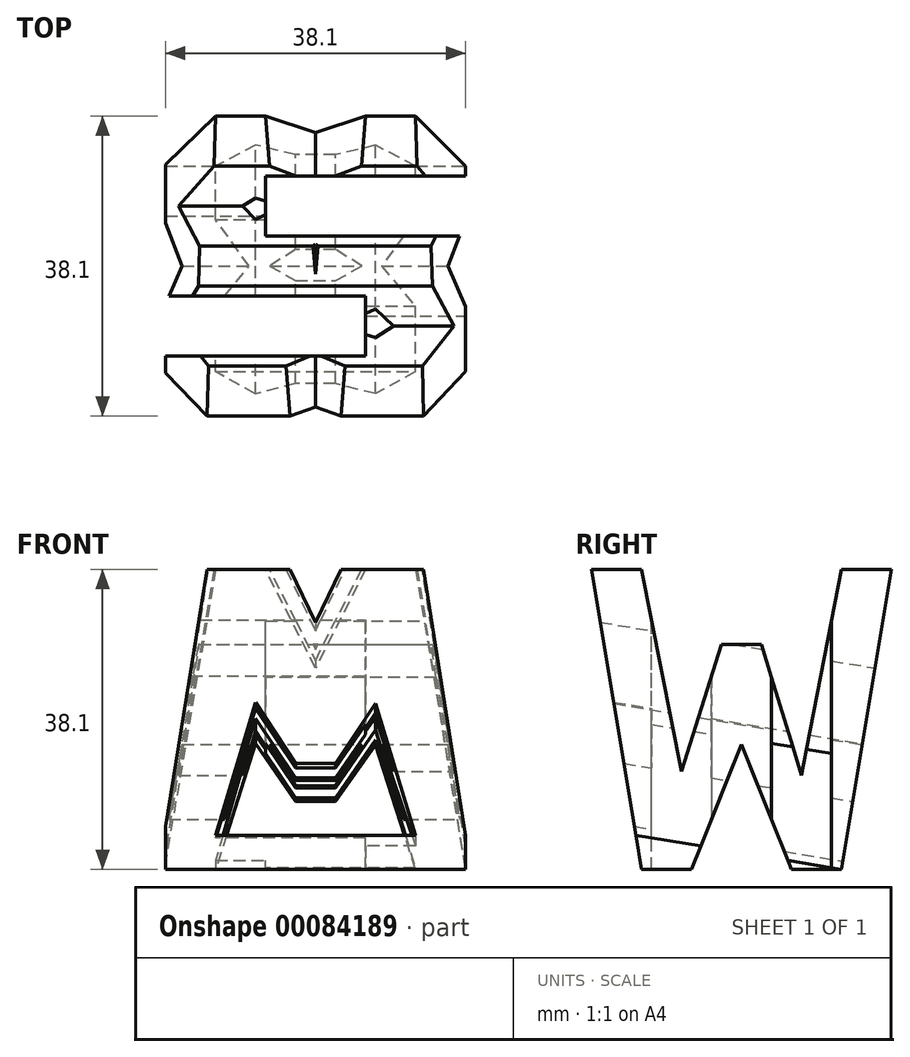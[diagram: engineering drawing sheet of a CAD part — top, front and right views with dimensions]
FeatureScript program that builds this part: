
annotation { "Feature Type Name" : "Feature", "Feature Type Description" : "" }
export const myFeature = defineFeature(function(context is Context, id is Id, definition is map)
    precondition{}
    {
        {
            var Q0;
            Q0=qCreatedBy(makeId("Front.planeOp"),FACE);
            var sketch = newSketch(context, id + "F0", { "sketchPlane" : qUnion([Q0])});
            skLineSegment(sketch, "E0", {"start": v(0, 0) * mm, "end": v(38.1, 0) * mm});
            skLineSegment(sketch, "E1", {"start": v(38.1, 0) * mm, "end": v(38.1, 38.1) * mm});
            skLineSegment(sketch, "E2", {"start": v(38.1, 38.1) * mm, "end": v(0, 38.1) * mm});
            skLineSegment(sketch, "E3", {"start": v(0, 38.1) * mm, "end": v(0, 0) * mm});
            skSolve(sketch);
        }
        {
            var Q0;
            Q0=makeQuery(id+"F0.imprint","IMPRINT",FACE,{"disambiguationData":[TD([[makeQuery(id+"F0.imprint","IMPRINT",EDGE,{"derivedFrom":sQuery(id+"F0.wireOp",EDGE,"E0")}),1.0]])]});
            extrude(context, id + "F1", {"entities" : qUnion([Q0]), "depth" : 38.1 * mm});
        }
        {
            var Q0;
            Q0=qCreatedBy(makeId("Top.planeOp"),FACE);
            cPlane(context, id + "F2", {"entities" : qUnion([Q0]), "cplaneType" : CPlaneType.OFFSET, "offset" : 38.1 * mm, "width" : 152.4 * mm, "height" : 152.4 * mm});
        }
        {
            var Q0;
            Q0=makeQuery(id+"F1.opExtrude","SWEPT_FACE",FACE,{"disambiguationData":[OSD([sQuery(id+"F0.wireOp",EDGE,"E1")])]});
            var sketch = newSketch(context, id + "F3", { "sketchPlane" : qUnion([Q0])});
            skLineSegment(sketch, "E4", {"start": v(-31.75, 38.1) * mm, "end": v(-26.67, 12.44) * mm});
            skLineSegment(sketch, "E5", {"start": v(-26.67, 12.44) * mm, "end": v(-21.6, 28.58) * mm});
            skLineSegment(sketch, "E6", {"start": v(-21.59, 28.58) * mm, "end": v(-16.5, 28.58) * mm});
            skLineSegment(sketch, "E7", {"start": v(-16.5, 28.58) * mm, "end": v(-11.43, 11.92) * mm});
            skLineSegment(sketch, "E8", {"start": v(-11.43, 11.92) * mm, "end": v(-6.35, 38.1) * mm});
            skLineSegment(sketch, "E9", {"start": v(-6.35, 38.1) * mm, "end": v(0, 38.1) * mm});
            skLineSegment(sketch, "E10", {"start": v(0, 38.1) * mm, "end": v(-6.35, 0) * mm});
            skLineSegment(sketch, "E11", {"start": v(-12.7, 0) * mm, "end": v(-19.05, 15.88) * mm});
            skPoint(sketch, "E11.endSnap0", {"position": v(-19.05, 0) * mm});
            skLineSegment(sketch, "E12", {"start": v(-19.05, 15.88) * mm, "end": v(-25.4, 0) * mm});
            skLineSegment(sketch, "E13", {"start": v(-31.75, 0) * mm, "end": v(-38.1, 38.1) * mm});
            skSolve(sketch);
        }
        {
            var Q0;
            {var subQ0=sQuery(id+"F3.wireOp",EDGE,"E4");Q0=makeQuery(id+"F3.imprint","IMPRINT",FACE,{"disambiguationData":[TD([[makeQuery(id+"F3.imprint","IMPRINT",EDGE,{"derivedFrom":subQ0}),1.0]])]});}
            var Q1;
            {var subQ0=sQuery(id+"F3.wireOp",EDGE,"E13");Q1=makeQuery(id+"F3.imprint","IMPRINT",FACE,{"disambiguationData":[TD([[makeQuery(id+"F3.imprint","IMPRINT",EDGE,{"derivedFrom":subQ0}),1.0]])]});}
            var Q2;
            {var subQ0=sQuery(id+"F3.wireOp",EDGE,"E11");Q2=makeQuery(id+"F3.imprint","IMPRINT",FACE,{"disambiguationData":[TD([[makeQuery(id+"F3.imprint","IMPRINT",EDGE,{"derivedFrom":subQ0}),1.0]])]});}
            var Q3;
            {var subQ0=sQuery(id+"F3.wireOp",EDGE,"E10");Q3=makeQuery(id+"F3.imprint","IMPRINT",FACE,{"disambiguationData":[TD([[makeQuery(id+"F3.imprint","IMPRINT",EDGE,{"derivedFrom":subQ0}),1.0]])]});}
            extrude(context, id + "F4", {"entities" : qUnion([Q0, Q1, Q2, Q3]), "operationType" : NewBodyOperationType.REMOVE, "oppositeDirection" : true, "depth" : 38.1 * mm});
        }
        {
            var Q0;
            Q0=makeQuery(id+"F4.boolean.opBoolean","COPY",FACE,{"derivedFrom":makeQuery(id+"F4.opExtrude","SWEPT_FACE",FACE,{"disambiguationData":[OSD([sQuery(id+"F3.wireOp",EDGE,"E10")])]})});
            var sketch = newSketch(context, id + "F5", { "sketchPlane" : qUnion([Q0])});
            skLineSegment(sketch, "E14", {"start": v(-25.4, 37.58) * mm, "end": v(-19.05, 24.9) * mm});
            skLineSegment(sketch, "E15", {"start": v(-19.05, 24.9) * mm, "end": v(-12.7, 37.58) * mm});
            skLineSegment(sketch, "E16", {"start": v(-6.35, 37.58) * mm, "end": v(0, 0) * mm});
            skLineSegment(sketch, "E17", {"start": v(0, 0) * mm, "end": v(0, -1.04) * mm});
            skLineSegment(sketch, "E18", {"start": v(-31.75, 37.58) * mm, "end": v(-38.1, -1.04) * mm});
            skLineSegment(sketch, "E19", {"start": v(-31.75, -1.04) * mm, "end": v(-26.67, 15) * mm});
            skLineSegment(sketch, "E20", {"start": v(-26.67, 15) * mm, "end": v(-21.59, 7.7) * mm});
            skLineSegment(sketch, "E21", {"start": v(-21.59, 7.7) * mm, "end": v(-16.5, 7.7) * mm});
            skLineSegment(sketch, "E22", {"start": v(-16.51, 7.7) * mm, "end": v(-11.43, 15.15) * mm});
            skLineSegment(sketch, "E23", {"start": v(-11.43, 15.15) * mm, "end": v(-6.35, -1.04) * mm});
            skSolve(sketch);
        }
        {
            var Q0;
            {var subQ0=sQuery(id+"F5.wireOp",EDGE,"E19");Q0=makeQuery(id+"F5.imprint","IMPRINT",FACE,{"disambiguationData":[TD([[makeQuery(id+"F5.imprint","IMPRINT",EDGE,{"derivedFrom":subQ0}),-1.0]])]});}
            var Q1;
            {var subQ0=sQuery(id+"F5.wireOp",EDGE,"E18");Q1=makeQuery(id+"F5.imprint","IMPRINT",FACE,{"disambiguationData":[TD([[makeQuery(id+"F5.imprint","IMPRINT",EDGE,{"derivedFrom":subQ0}),-1.0]])]});}
            var Q2;
            {var subQ0=sQuery(id+"F5.wireOp",EDGE,"E14");Q2=makeQuery(id+"F5.imprint","IMPRINT",FACE,{"disambiguationData":[TD([[makeQuery(id+"F5.imprint","IMPRINT",EDGE,{"derivedFrom":subQ0}),1.0]])]});}
            var Q3;
            {var subQ0=sQuery(id+"F5.wireOp",EDGE,"E16");Q3=makeQuery(id+"F5.imprint","IMPRINT",FACE,{"disambiguationData":[TD([[makeQuery(id+"F5.imprint","IMPRINT",EDGE,{"derivedFrom":subQ0}),1.0]])]});}
            extrude(context, id + "F6", {"entities" : qUnion([Q0, Q1, Q2, Q3]), "operationType" : NewBodyOperationType.REMOVE, "oppositeDirection" : true, "depth" : 38.1 * mm});
        }
        {
            var Q0;
            Q0=qCreatedBy(id+"F2.planeOp",FACE);
            var sketch = newSketch(context, id + "F7", { "sketchPlane" : qUnion([Q0])});
            skLineSegment(sketch, "E24", {"start": v(38.1, 0) * mm, "end": v(38.1, -38.1) * mm});
            skLineSegment(sketch, "E25", {"start": v(38.1, -38.1) * mm, "end": v(0, -38.1) * mm});
            skLineSegment(sketch, "E26", {"start": v(0, -38.1) * mm, "end": v(0, 0) * mm});
            skLineSegment(sketch, "E27", {"start": v(0, 0) * mm, "end": v(38.1, 0) * mm});
            skLineSegment(sketch, "E28", {"start": v(38.1, -7.62) * mm, "end": v(12.7, -7.62) * mm});
            skLineSegment(sketch, "E29", {"start": v(12.7, -7.62) * mm, "end": v(12.7, -15.24) * mm});
            skLineSegment(sketch, "E30", {"start": v(0, -22.86) * mm, "end": v(25.4, -22.86) * mm});
            skLineSegment(sketch, "E31", {"start": v(25.4, -22.86) * mm, "end": v(25.4, -30.48) * mm});
            skLineSegment(sketch, "E32", {"start": v(25.4, -30.48) * mm, "end": v(0, -30.48) * mm});
            skLineSegment(sketch, "E33", {"start": v(12.7, -15.24) * mm, "end": v(38.1, -15.24) * mm});
            skSolve(sketch);
        }
        {
            var Q0;
            {var subQ0=sQuery(id+"F7.wireOp",EDGE,"E28");Q0=makeQuery(id+"F7.imprint","IMPRINT",FACE,{"disambiguationData":[TD([[makeQuery(id+"F7.imprint","IMPRINT",EDGE,{"derivedFrom":subQ0}),1.0]])]});}
            var Q1;
            {var subQ0=sQuery(id+"F7.wireOp",EDGE,"E30");Q1=makeQuery(id+"F7.imprint","IMPRINT",FACE,{"disambiguationData":[TD([[makeQuery(id+"F7.imprint","IMPRINT",EDGE,{"derivedFrom":subQ0}),-1.0]])]});}
            extrude(context, id + "F8", {"entities" : qUnion([Q0, Q1]), "operationType" : NewBodyOperationType.REMOVE, "oppositeDirection" : true, "depth" : 38.1 * mm});
        }
    });
